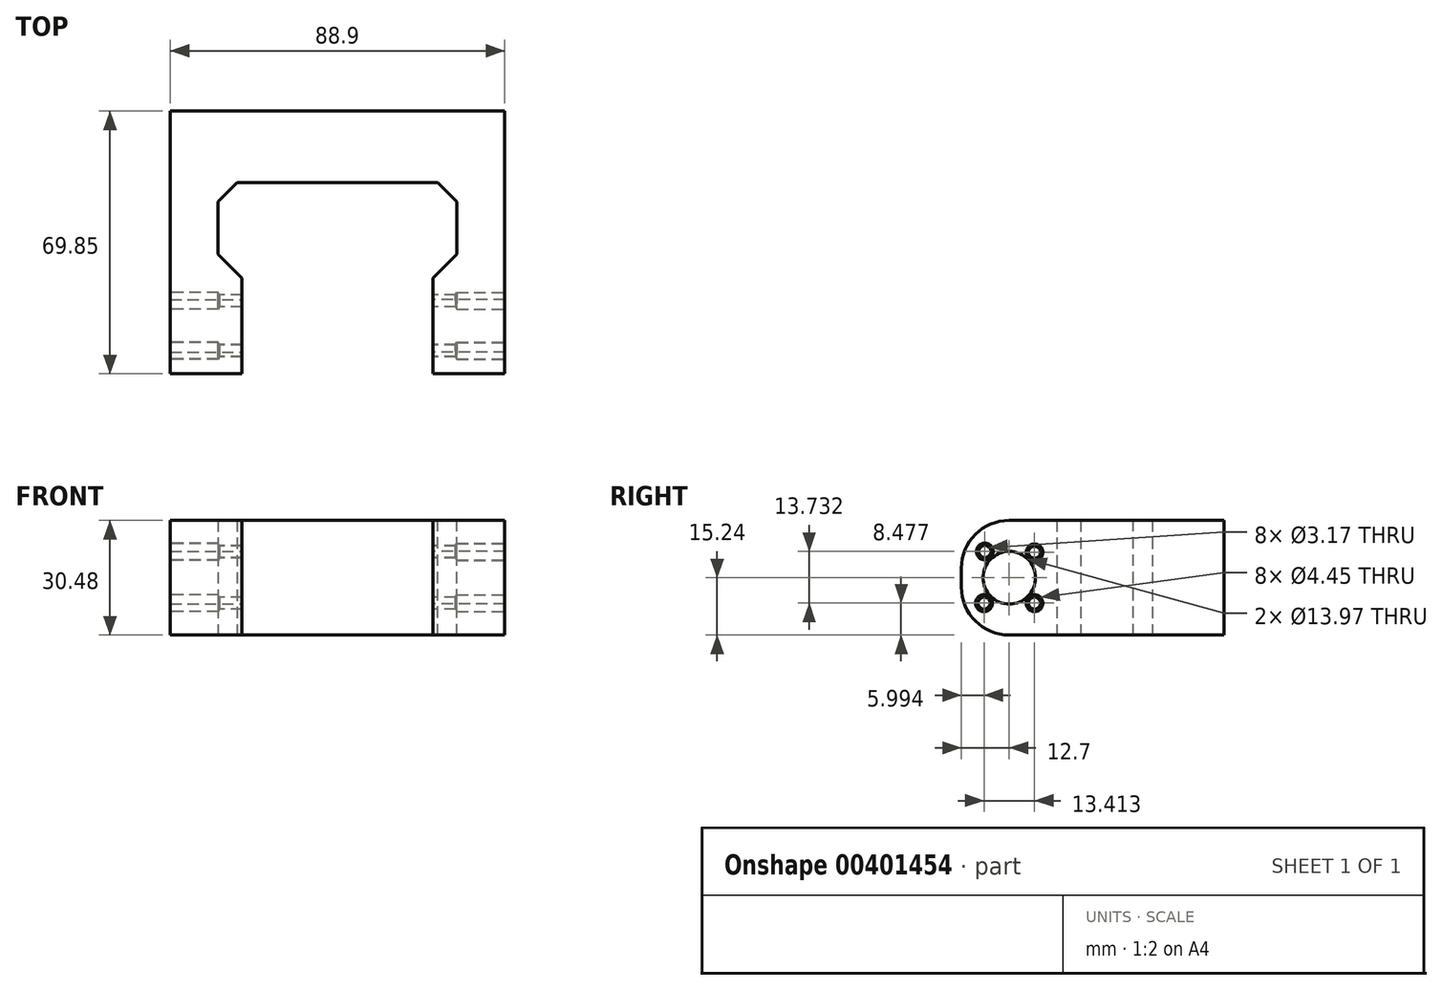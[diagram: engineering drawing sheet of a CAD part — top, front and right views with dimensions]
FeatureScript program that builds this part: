
annotation { "Feature Type Name" : "Feature", "Feature Type Description" : "" }
export const myFeature = defineFeature(function(context is Context, id is Id, definition is map)
    precondition{}
    {
        {
            var Q0;
            Q0=qCreatedBy(makeId("Top.planeOp"),FACE);
            var sketch = newSketch(context, id + "F0", { "sketchPlane" : qUnion([Q0])});
            skLineSegment(sketch, "E0", {"start": v(-50.8, 57.15) * mm, "end": v(-50.8, -12.7) * mm});
            skLineSegment(sketch, "E1", {"start": v(38.1, 57.15) * mm, "end": v(38.1, -12.7) * mm});
            skLineSegment(sketch, "E2", {"start": v(-50.8, -12.7) * mm, "end": v(-31.75, -12.7) * mm});
            skLineSegment(sketch, "E3", {"start": v(38.1, -12.7) * mm, "end": v(19.05, -12.7) * mm});
            skLineSegment(sketch, "E4", {"start": v(-31.75, -12.7) * mm, "end": v(-31.75, 12.7) * mm});
            skLineSegment(sketch, "E5", {"start": v(19.05, -12.7) * mm, "end": v(19.05, 12.7) * mm});
            skLineSegment(sketch, "E6", {"start": v(-31.75, 12.7) * mm, "end": v(-38.1, 12.7) * mm});
            skLineSegment(sketch, "E7", {"start": v(19.05, 12.7) * mm, "end": v(25.4, 12.7) * mm});
            skLineSegment(sketch, "E8", {"start": v(-38.1, 12.7) * mm, "end": v(-38.1, 38.1) * mm});
            skLineSegment(sketch, "E9", {"start": v(-50.8, 57.15) * mm, "end": v(38.1, 57.15) * mm});
            skLineSegment(sketch, "E10", {"start": v(25.4, 12.7) * mm, "end": v(25.4, 38.1) * mm});
            skLineSegment(sketch, "E11", {"start": v(-38.1, 38.1) * mm, "end": v(25.4, 38.1) * mm});
            skPoint(sketch, "E12.endSnap0", {"position": v(19.05, 0) * mm});
            skSolve(sketch);
        }
        {
            var Q0;
            Q0=makeQuery(id+"F0.imprint","IMPRINT",FACE,{"disambiguationData":[TD([[makeQuery(id+"F0.imprint","IMPRINT",EDGE,{"derivedFrom":sQuery(id+"F0.wireOp",EDGE,"E0")}),1.0]])]});
            var Q1;
            Q1 = qSketchRegion(id + "FaKLC1ZL99H1EX4_1", true);
            extrude(context, id + "F1", {"entities" : qUnion([Q0, Q1]), "depth" : 30.48 * mm});
        }
        {
            var Q0;
            Q0=makeQuery(id+"F1.opExtrude","SWEPT_FACE",FACE,{"disambiguationData":[OSD([sQuery(id+"F0.wireOp",EDGE,"E4")])]});
            var sketch = newSketch(context, id + "F2", { "sketchPlane" : qUnion([Q0])});
            skLineSegment(sketch, "E13", {"start": v(0, 0) * mm, "end": v(0, 15.24) * mm});
            skSolve(sketch);
        }
        {
            var Q0;
            Q0=makeQuery(id+"F1.opExtrude","SWEPT_FACE",FACE,{"disambiguationData":[OSD([sQuery(id+"F0.wireOp",EDGE,"E5")])]});
            var sketch = newSketch(context, id + "F3", { "sketchPlane" : qUnion([Q0])});
            skLineSegment(sketch, "E14", {"start": v(0, 0) * mm, "end": v(0, 15.24) * mm});
            skCircle(sketch, "E15", {"center": v(0, 15.24) * mm, "radius": 7.62 * mm});
            skSolve(sketch);
        }
        {
            var Q0;
            Q0=sQuery(id+"F3.wireOp",VERTEX,"E15.center");
            var Q1;
            Q1=sQuery(id+"F2.wireOp",VERTEX,"E13.end");
            var Q2;
            Q2=makeQuery(id+"F1.opExtrude","SWEPT_BODY",BODY,{"disambiguationData":[OSD([sQuery(id+"F0.wireOp",EDGE,"E0"),sQuery(id+"F0.wireOp",EDGE,"E1"),sQuery(id+"F0.wireOp",EDGE,"E2"),sQuery(id+"F0.wireOp",EDGE,"E3"),sQuery(id+"F0.wireOp",EDGE,"E4"),sQuery(id+"F0.wireOp",EDGE,"E5"),sQuery(id+"F0.wireOp",EDGE,"E6"),sQuery(id+"F0.wireOp",EDGE,"E7"),sQuery(id+"F0.wireOp",EDGE,"E8"),sQuery(id+"F0.wireOp",EDGE,"E9"),sQuery(id+"F0.wireOp",EDGE,"E10"),sQuery(id+"F0.wireOp",EDGE,"E11")])]});
            hole(context, id + "F4", {"style" : HoleStyle.SIMPLE, "endStyle" : HoleEndStyle.THROUGH, "holeDiameter" : 13.97 * mm, "isTappedThrough" : true, "tappedDepth" : 12.7 * mm, "tapClearance" : 3, "locations" : qUnion([Q0, Q1]), "scope" : qUnion([Q2])});
        }
        {
            var Q0;
            Q0=makeQuery(id+"F1.opExtrude","SWEPT_FACE",FACE,{"disambiguationData":[OSD([sQuery(id+"F0.wireOp",EDGE,"E0")])]});
            var sketch = newSketch(context, id + "F5", { "sketchPlane" : qUnion([Q0])});
            skLineSegment(sketch, "E16.bottom", {"start": v(9.53, 24.77) * mm, "end": v(-9.52, 24.77) * mm});
            skLineSegment(sketch, "E16.top", {"start": v(9.53, 5.72) * mm, "end": v(-9.52, 5.71) * mm});
            skLineSegment(sketch, "E16.left", {"start": v(9.53, 24.77) * mm, "end": v(9.53, 5.72) * mm});
            skLineSegment(sketch, "E16.right", {"start": v(-9.52, 24.77) * mm, "end": v(-9.52, 5.71) * mm});
            skPoint(sketch, "E16.middle", {"position": v(0, 15.24) * mm});
            skLineSegment(sketch, "E17", {"start": v(-4.44, 10.7) * mm, "end": v(-5.57, 9.59) * mm});
            skLineSegment(sketch, "E18", {"start": v(-5.57, 9.59) * mm, "end": v(-6.7, 8.48) * mm});
            skCircle(sketch, "E19", {"center": v(-6.7, 8.48) * mm, "radius": 1.59 * mm});
            skPoint(sketch, "E20.startSnap0", {"position": v(0, 5.71) * mm});
            skPoint(sketch, "E20.endSnap0", {"position": v(0, 5.71) * mm});
            skCircle(sketch, "E21.MirrorC", {"center": v(-6.7, 22) * mm, "radius": 1.59 * mm});
            skLineSegment(sketch, "E22.MirrorCS", {"start": v(-5.57, 20.9) * mm, "end": v(-6.7, 22) * mm});
            skLineSegment(sketch, "E23.MirrorCS", {"start": v(-4.44, 19.78) * mm, "end": v(-5.57, 20.9) * mm});
            skLineSegment(sketch, "E24.MirrorCS", {"start": v(4.44, 10.7) * mm, "end": v(5.57, 9.59) * mm});
            skLineSegment(sketch, "E25.MirrorCS", {"start": v(5.57, 9.59) * mm, "end": v(6.7, 8.48) * mm});
            skCircle(sketch, "E26.MirrorC", {"center": v(6.7, 8.48) * mm, "radius": 1.59 * mm});
            skLineSegment(sketch, "E27.MirrorCS", {"start": v(4.36, 19.86) * mm, "end": v(5.43, 21.03) * mm});
            skLineSegment(sketch, "E28.MirrorCS", {"start": v(5.43, 21.03) * mm, "end": v(6.5, 22.2) * mm});
            skPoint(sketch, "E29.MirrorP", {"position": v(9.09, 15.16) * mm});
            skLineSegment(sketch, "E30.MirrorCS", {"start": v(3.93, 19.4) * mm, "end": v(5, 20.58) * mm});
            skCircle(sketch, "E31.MirrorC", {"center": v(6.07, 21.76) * mm, "radius": 1.59 * mm});
            skLineSegment(sketch, "E32.MirrorCS", {"start": v(5, 20.58) * mm, "end": v(6.07, 21.76) * mm});
            skCircle(sketch, "E33", {"center": v(0, 15.24) * mm, "radius": 6.35 * mm});
            skSolve(sketch);
        }
        {
            var Q0;
            Q0=sQuery(id+"F5.wireOp",VERTEX,"E22.MirrorCS.end");
            var Q1;
            Q1=sQuery(id+"F5.wireOp",VERTEX,"E28.MirrorCS.end");
            var Q2;
            Q2=sQuery(id+"F5.wireOp",VERTEX,"E25.MirrorCS.end");
            var Q3;
            Q3=sQuery(id+"F5.wireOp",VERTEX,"E19.center");
            var Q4;
            Q4=makeQuery(id+"F1.opExtrude","SWEPT_BODY",BODY,{"disambiguationData":[OSD([sQuery(id+"F0.wireOp",EDGE,"E0"),sQuery(id+"F0.wireOp",EDGE,"E1"),sQuery(id+"F0.wireOp",EDGE,"E2"),sQuery(id+"F0.wireOp",EDGE,"E3"),sQuery(id+"F0.wireOp",EDGE,"E4"),sQuery(id+"F0.wireOp",EDGE,"E5"),sQuery(id+"F0.wireOp",EDGE,"E6"),sQuery(id+"F0.wireOp",EDGE,"E7"),sQuery(id+"F0.wireOp",EDGE,"E8"),sQuery(id+"F0.wireOp",EDGE,"E9"),sQuery(id+"F0.wireOp",EDGE,"E10"),sQuery(id+"F0.wireOp",EDGE,"E11")])]});
            hole(context, id + "F6", {"style" : HoleStyle.SIMPLE, "endStyle" : HoleEndStyle.THROUGH, "holeDiameter" : 3.17 * mm, "isTappedThrough" : true, "tappedDepth" : 12.7 * mm, "tapClearance" : 3, "locations" : qUnion([Q0, Q1, Q2, Q3]), "scope" : qUnion([Q4])});
        }
        {
            var Q0;
            Q0=makeQuery(id+"F1.opExtrude","SWEPT_FACE",FACE,{"disambiguationData":[OSD([sQuery(id+"F0.wireOp",EDGE,"E9")])]});
            var sketch = newSketch(context, id + "F7", { "sketchPlane" : qUnion([Q0])});
            skLineSegment(sketch, "E34.bottom", {"start": v(33.05, 25.53) * mm, "end": v(-20.35, 25.53) * mm});
            skLineSegment(sketch, "E34.top", {"start": v(33.05, 4.95) * mm, "end": v(-20.35, 4.95) * mm});
            skLineSegment(sketch, "E34.left", {"start": v(33.05, 25.53) * mm, "end": v(33.05, 4.95) * mm});
            skLineSegment(sketch, "E34.right", {"start": v(-20.35, 25.53) * mm, "end": v(-20.35, 4.95) * mm});
            skPoint(sketch, "E34.middle", {"position": v(6.35, 15.24) * mm});
            skLineSegment(sketch, "E35", {"start": v(-20.35, 25.53) * mm, "end": v(-38.1, 30.48) * mm});
            skLineSegment(sketch, "E36", {"start": v(33.05, 25.53) * mm, "end": v(50.8, 30.48) * mm});
            skSolve(sketch);
        }
        {
            var Q0;
            {var subQ0=sQuery(id+"F0.wireOp",EDGE,"E10");Q0=makeQuery(id+"FXZxjuzA8l6YYxy_1.boolean.opBoolean","SPLIT",EDGE,{"disambiguationData":[topologyDisambiguationEdgeConnected([makeQuery(id+"F1.opExtrude","SWEPT_FACE",FACE,{"disambiguationData":[OSD([subQ0])]}),makeQuery(id+"FXZxjuzA8l6YYxy_1.opExtrude","SWEPT_FACE",FACE,{"disambiguationData":[OSD([sQuery(id+"FlGbEd74mKDDrFE_1.wireOp",EDGE,"SaYC0krj-LSic-8kc4-WGOC-20uy2zf9MN4h.left")])]})])],"derivedFrom":makeQuery(id+"F1.opExtrude","SWEPT_EDGE",EDGE,{"disambiguationData":[OSD([subQ0,sQuery(id+"F0.wireOp",EDGE,"E11")])]})});}
            var Q1;
            Q1=makeQuery(id+"F1.opExtrude","SWEPT_EDGE",EDGE,{"disambiguationData":[OSD([sQuery(id+"F0.wireOp",EDGE,"E8"),sQuery(id+"F0.wireOp",EDGE,"E11")])]});
            chamfer(context, id + "F8", {"entities" : qUnion([Q0, Q1]), "width" : 5.08 * mm, "tangentPropagation" : true});
        }
        {
            var Q0;
            Q0=makeQuery(id+"F1.opExtrude","SWEPT_EDGE",EDGE,{"disambiguationData":[OSD([sQuery(id+"F0.wireOp",EDGE,"E7"),sQuery(id+"F0.wireOp",EDGE,"E10")])]});
            var Q1;
            Q1=makeQuery(id+"F1.opExtrude","SWEPT_EDGE",EDGE,{"disambiguationData":[OSD([sQuery(id+"F0.wireOp",EDGE,"E6"),sQuery(id+"F0.wireOp",EDGE,"E8")])]});
            chamfer(context, id + "F9", {"entities" : qUnion([Q0, Q1]), "width" : 6.35 * mm, "tangentPropagation" : true});
        }
        {
            var Q0;
            Q0=sQuery(id+"F5.wireOp",VERTEX,"E28.MirrorCS.end");
            var Q1;
            Q1=sQuery(id+"F5.wireOp",VERTEX,"E26.MirrorC.center");
            var Q2;
            Q2=sQuery(id+"F5.wireOp",VERTEX,"E19.center");
            var Q3;
            Q3=sQuery(id+"F5.wireOp",VERTEX,"E22.MirrorCS.end");
            var Q4;
            Q4=makeQuery(id+"F1.opExtrude","SWEPT_BODY",BODY,{"disambiguationData":[OSD([sQuery(id+"F0.wireOp",EDGE,"E0"),sQuery(id+"F0.wireOp",EDGE,"E1"),sQuery(id+"F0.wireOp",EDGE,"E2"),sQuery(id+"F0.wireOp",EDGE,"E3"),sQuery(id+"F0.wireOp",EDGE,"E4"),sQuery(id+"F0.wireOp",EDGE,"E5"),sQuery(id+"F0.wireOp",EDGE,"E6"),sQuery(id+"F0.wireOp",EDGE,"E7"),sQuery(id+"F0.wireOp",EDGE,"E8"),sQuery(id+"F0.wireOp",EDGE,"E9"),sQuery(id+"F0.wireOp",EDGE,"E10"),sQuery(id+"F0.wireOp",EDGE,"E11")])]});
            hole(context, id + "F10", {"style" : HoleStyle.SIMPLE, "endStyle" : HoleEndStyle.BLIND, "holeDiameter" : 4.44 * mm, "holeDepth" : 12.7 * mm, "isTappedThrough" : true, "tappedDepth" : 12.7 * mm, "tapClearance" : 3, "locations" : qUnion([Q0, Q1, Q2, Q3]), "scope" : qUnion([Q4])});
        }
        {
            var Q0;
            Q0=makeQuery(id+"F1.opExtrude","SWEPT_FACE",FACE,{"disambiguationData":[OSD([sQuery(id+"F0.wireOp",EDGE,"E1")])]});
            var sketch = newSketch(context, id + "F11", { "sketchPlane" : qUnion([Q0])});
            skPoint(sketch, "E37.0", {"position": v(6.7, 22) * mm});
            skPoint(sketch, "E37.1", {"position": v(6.7, 8.48) * mm});
            skPoint(sketch, "E37.2", {"position": v(-6.7, 8.48) * mm});
            skPoint(sketch, "E37.3", {"position": v(-6.5, 22.2) * mm});
            skSolve(sketch);
        }
        {
            var Q0;
            Q0=sQuery(id+"F11.wireOp",VERTEX,"E37.2");
            var Q1;
            Q1=sQuery(id+"F11.wireOp",VERTEX,"E37.3");
            var Q2;
            Q2=sQuery(id+"F11.wireOp",VERTEX,"E37.0");
            var Q3;
            Q3=sQuery(id+"F11.wireOp",VERTEX,"E37.1");
            var Q4;
            Q4=makeQuery(id+"F1.opExtrude","SWEPT_BODY",BODY,{"disambiguationData":[OSD([sQuery(id+"F0.wireOp",EDGE,"E0"),sQuery(id+"F0.wireOp",EDGE,"E1"),sQuery(id+"F0.wireOp",EDGE,"E2"),sQuery(id+"F0.wireOp",EDGE,"E3"),sQuery(id+"F0.wireOp",EDGE,"E4"),sQuery(id+"F0.wireOp",EDGE,"E5"),sQuery(id+"F0.wireOp",EDGE,"E6"),sQuery(id+"F0.wireOp",EDGE,"E7"),sQuery(id+"F0.wireOp",EDGE,"E8"),sQuery(id+"F0.wireOp",EDGE,"E9"),sQuery(id+"F0.wireOp",EDGE,"E10"),sQuery(id+"F0.wireOp",EDGE,"E11")])]});
            hole(context, id + "F12", {"style" : HoleStyle.SIMPLE, "endStyle" : HoleEndStyle.BLIND, "holeDiameter" : 4.44 * mm, "holeDepth" : 12.7 * mm, "isTappedThrough" : true, "tappedDepth" : 12.7 * mm, "tapClearance" : 3, "locations" : qUnion([Q0, Q1, Q2, Q3]), "scope" : qUnion([Q4])});
        }
        {
            var Q0;
            Q0=makeQuery(id+"F1.opExtrude","CAP_EDGE",EDGE,{"disambiguationData":[OSD([sQuery(id+"F0.wireOp",EDGE,"E2")])],"isStart":false});
            var Q1;
            Q1=makeQuery(id+"F1.opExtrude","CAP_EDGE",EDGE,{"disambiguationData":[OSD([sQuery(id+"F0.wireOp",EDGE,"E3")])],"isStart":false});
            var Q2;
            Q2=makeQuery(id+"F1.opExtrude","CAP_EDGE",EDGE,{"disambiguationData":[OSD([sQuery(id+"F0.wireOp",EDGE,"E3")])],"isStart":true});
            var Q3;
            Q3=makeQuery(id+"F1.opExtrude","CAP_EDGE",EDGE,{"disambiguationData":[OSD([sQuery(id+"F0.wireOp",EDGE,"E2")])],"isStart":true});
            fillet(context, id + "F13", {"entities" : qUnion([Q0, Q1, Q2, Q3]), "radius" : 12.7 * mm, "tangentPropagation" : true, "allowEdgeOverflow" : false});
        }
    });
